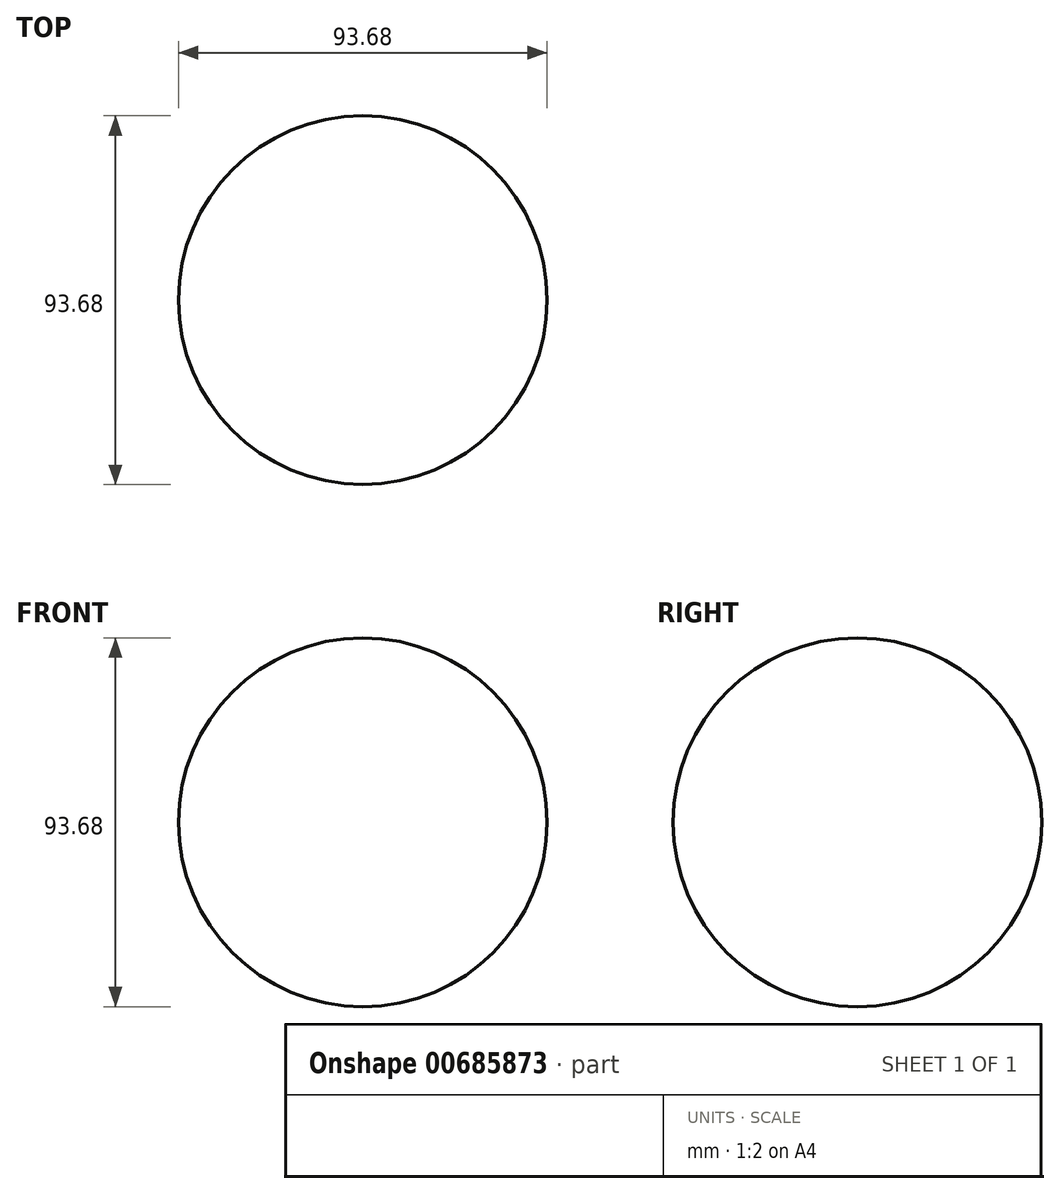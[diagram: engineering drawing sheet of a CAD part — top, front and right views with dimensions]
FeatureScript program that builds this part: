
annotation { "Feature Type Name" : "Feature", "Feature Type Description" : "" }
export const myFeature = defineFeature(function(context is Context, id is Id, definition is map)
    precondition{}
    {
        {
            var Q0;
            Q0=qCreatedBy(makeId("Front.planeOp"),FACE);
            var sketch = newSketch(context, id + "F0", { "sketchPlane" : qUnion([Q0])});
            skArc(sketch, "E0", {"start": v(0, -46.84) * mm, "mid": v(46.84, 0) * mm, "end": v(0, 46.84) * mm});
            skLineSegment(sketch, "E1", {"start": v(0, 46.84) * mm, "end": v(0, -46.84) * mm});
            skSolve(sketch);
        }
        {
            var Q0;
            Q0=makeQuery(id+"F0.imprint","IMPRINT",FACE,{"disambiguationData":[TD([[makeQuery(id+"F0.imprint","IMPRINT",EDGE,{"derivedFrom":sQuery(id+"F0.wireOp",EDGE,"E0")}),1.0]])]});
            var Q1;
            Q1=sQuery(id+"F0.wireOp",EDGE,"E1");
            revolve(context, id + "F1", {"entities" : qUnion([Q0]), "axis" : qUnion([Q1]), "revolveType" : RevolveType.FULL});
        }
    });
